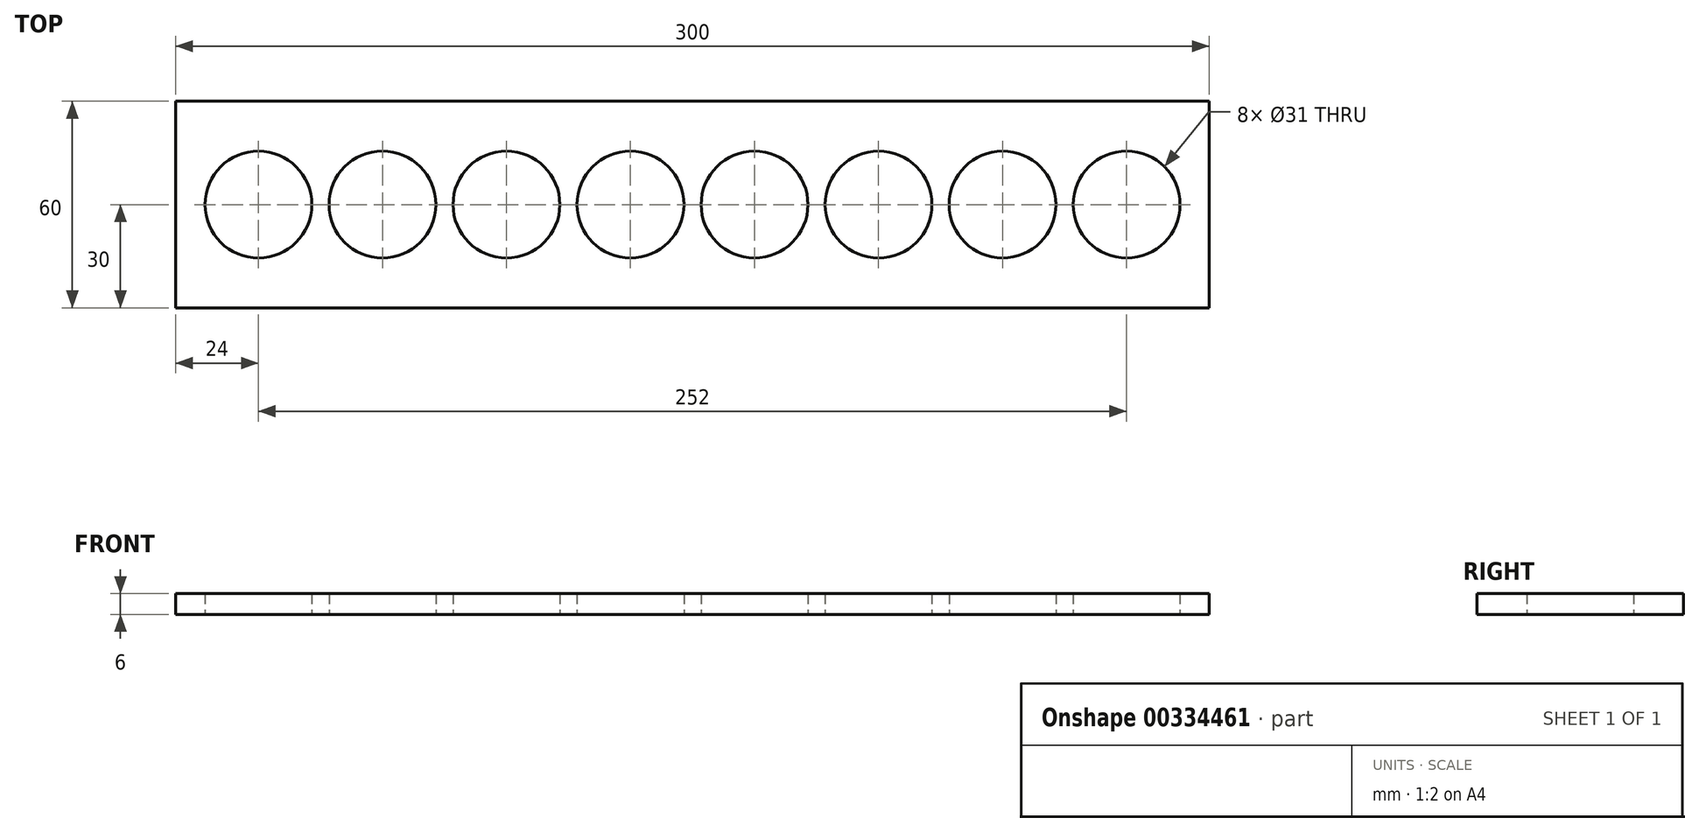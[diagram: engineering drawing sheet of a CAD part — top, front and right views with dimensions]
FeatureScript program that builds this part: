
annotation { "Feature Type Name" : "Feature", "Feature Type Description" : "" }
export const myFeature = defineFeature(function(context is Context, id is Id, definition is map)
    precondition{}
    {
        {
            var Q0;
            Q0=qCreatedBy(makeId("Top.planeOp"),FACE);
            var sketch = newSketch(context, id + "F0", { "sketchPlane" : qUnion([Q0])});
            skLineSegment(sketch, "E0", {"start": v(0, 0) * mm, "end": v(2.5, 0) * mm, "construction": true});
            skLineSegment(sketch, "E1", {"start": v(2.5, 0) * mm, "end": v(18, 0) * mm, "construction": true});
            skCircle(sketch, "E2", {"center": v(18, 0) * mm, "radius": 15.5 * mm});
            skCircle(sketch, "E3.1.0.0", {"center": v(54, 0) * mm, "radius": 15.5 * mm});
            skCircle(sketch, "E3.2.0.0", {"center": v(90, 0) * mm, "radius": 15.5 * mm});
            skCircle(sketch, "E3.3.0.0", {"center": v(126, 0) * mm, "radius": 15.5 * mm});
            skLineSegment(sketch, "E3.direction1", {"start": v(18, 0) * mm, "end": v(54, 0) * mm, "construction": true});
            skLineSegment(sketch, "E4", {"start": v(0, 0) * mm, "end": v(0, 20.1) * mm, "construction": true});
            skCircle(sketch, "E5.MirrorC", {"center": v(-54, 0) * mm, "radius": 15.5 * mm});
            skCircle(sketch, "E6.MirrorC", {"center": v(-90, 0) * mm, "radius": 15.5 * mm});
            skCircle(sketch, "E7.MirrorC", {"center": v(-126, 0) * mm, "radius": 15.5 * mm});
            skLineSegment(sketch, "E8.MirrorCS", {"start": v(-18, 0) * mm, "end": v(-54, 0) * mm, "construction": true});
            skCircle(sketch, "E9.MirrorC", {"center": v(-18, 0) * mm, "radius": 15.5 * mm});
            skLineSegment(sketch, "E10.bottom", {"start": v(150, 30) * mm, "end": v(-150, 30) * mm});
            skLineSegment(sketch, "E10.top", {"start": v(150, -30) * mm, "end": v(-150, -30) * mm});
            skLineSegment(sketch, "E10.left", {"start": v(150, 30) * mm, "end": v(150, -30) * mm});
            skLineSegment(sketch, "E10.right", {"start": v(-150, 30) * mm, "end": v(-150, -30) * mm});
            skPoint(sketch, "E10.middle", {"position": v(0, 0) * mm});
            skSolve(sketch);
        }
        {
            var Q0;
            Q0=makeQuery(id+"F0.imprint","IMPRINT",FACE,{"disambiguationData":[TD([[makeQuery(id+"F0.imprint","IMPRINT",EDGE,{"derivedFrom":sQuery(id+"F0.wireOp",EDGE,"E2")}),-1.0]])]});
            extrude(context, id + "F1", {"entities" : qUnion([Q0]), "depth" : 6 * mm});
        }
    });
